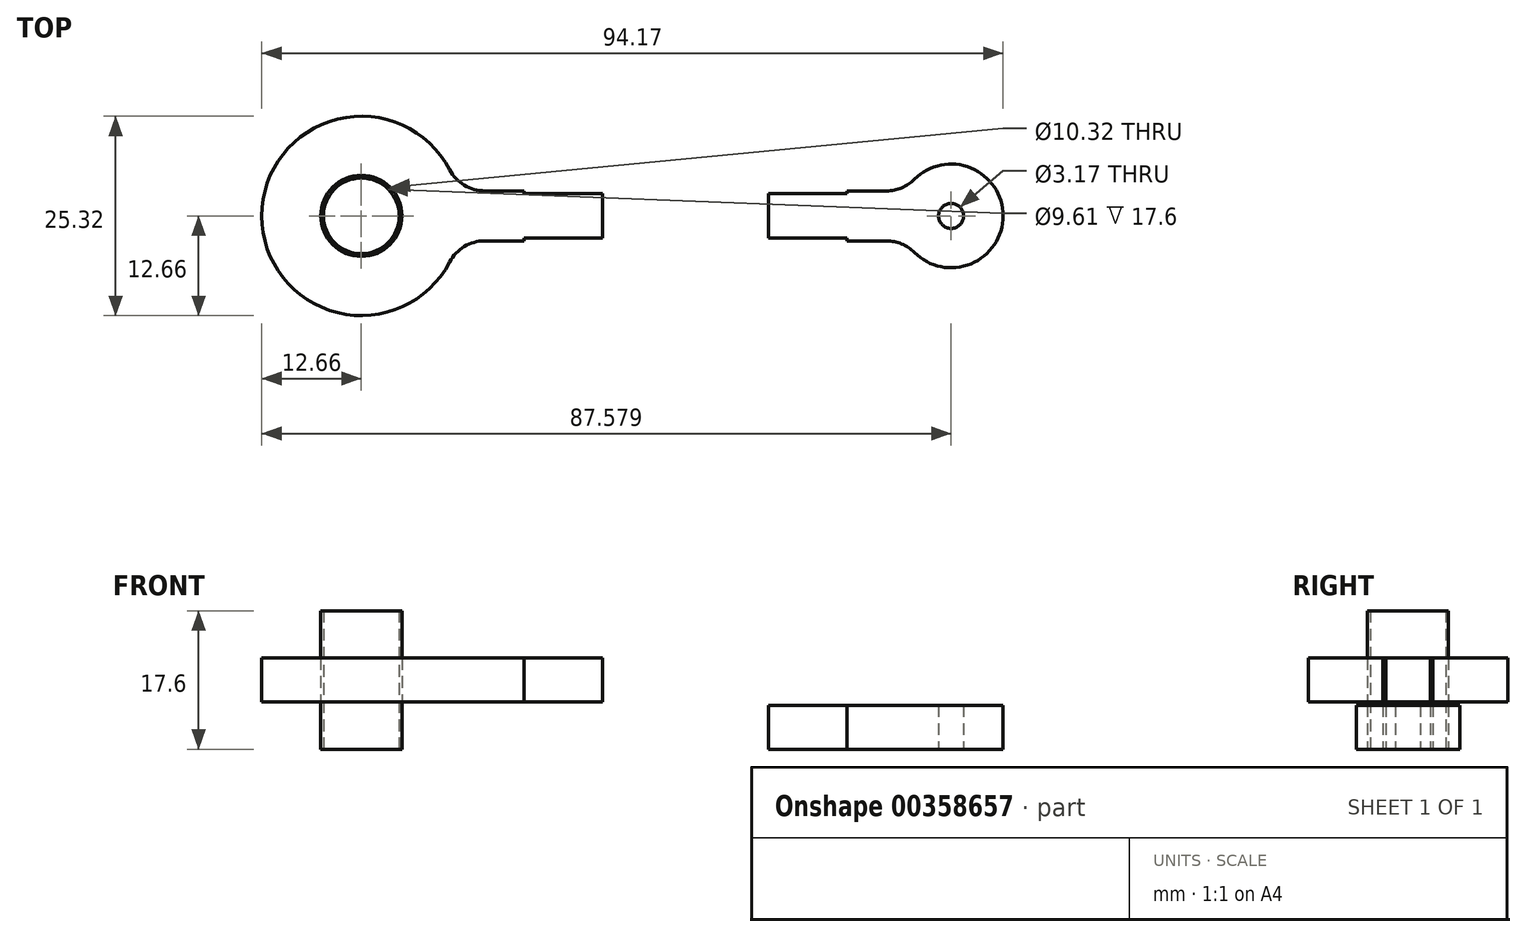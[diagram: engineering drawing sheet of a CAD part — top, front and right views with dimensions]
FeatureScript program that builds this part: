
annotation { "Feature Type Name" : "Feature", "Feature Type Description" : "" }
export const myFeature = defineFeature(function(context is Context, id is Id, definition is map)
    precondition{}
    {
        {
            var Q0;
            Q0=qCreatedBy(makeId("Top.planeOp"),FACE);
            var sketch = newSketch(context, id + "F0", { "sketchPlane" : qUnion([Q0])});
            skCircle(sketch, "E0", {"center": v(0, 0) * mm, "radius": 4.8 * mm});
            skCircle(sketch, "E1", {"center": v(0, 0) * mm, "radius": 5.16 * mm});
            skSolve(sketch);
        }
        {
            var Q0;
            Q0 = qSketchRegion(id + "F0", true);
            extrude(context, id + "F1", {"entities" : qUnion([Q0]), "depth" : (5.6 + 3 * 2 + 3 * 2) * mm, "offsetDistance" : 25 * mm});
        }
        {
            var Q0;
            Q0=qCreatedBy(makeId("Top.planeOp"),FACE);
            var sketch = newSketch(context, id + "F2", { "sketchPlane" : qUnion([Q0])});
            skCircle(sketch, "E2", {"center": v(0, 0) * mm, "radius": 5.16 * mm});
            skArc(sketch, "E3", {"start": v(11.22, 5.86) * mm, "mid": v(-12.66, 0) * mm, "end": v(11.22, -5.86) * mm});
            skLineSegment(sketch, "E4", {"start": v(0, 0) * mm, "end": v(90.69, 0) * mm, "construction": true});
            skLineSegment(sketch, "E5", {"start": v(15.65, 3.17) * mm, "end": v(20.65, 3.17) * mm});
            skLineSegment(sketch, "E6", {"start": v(20.65, 3.18) * mm, "end": v(20.65, 2.82) * mm});
            skLineSegment(sketch, "E7", {"start": v(20.65, 2.82) * mm, "end": v(30.65, 2.82) * mm});
            skLineSegment(sketch, "E8", {"start": v(30.65, 2.82) * mm, "end": v(30.65, -2.82) * mm});
            skLineSegment(sketch, "E9", {"start": v(30.65, -2.82) * mm, "end": v(20.65, -2.82) * mm});
            skLineSegment(sketch, "E10", {"start": v(20.65, -2.82) * mm, "end": v(20.65, -3.17) * mm});
            skLineSegment(sketch, "E11", {"start": v(20.65, -3.17) * mm, "end": v(15.65, -3.17) * mm});
            skArc(sketch, "E12", {"start": v(11.22, 5.86) * mm, "mid": v(13.06, 3.9) * mm, "end": v(15.65, 3.18) * mm});
            skArc(sketch, "E13", {"start": v(15.65, -3.17) * mm, "mid": v(13.06, -3.9) * mm, "end": v(11.22, -5.86) * mm});
            skLineSegment(sketch, "E14", {"start": v(51.7, 2.82) * mm, "end": v(61.7, 2.82) * mm});
            skLineSegment(sketch, "E15", {"start": v(51.7, -2.82) * mm, "end": v(61.7, -2.82) * mm});
            skLineSegment(sketch, "E16", {"start": v(61.7, -3.17) * mm, "end": v(66.7, -3.17) * mm});
            skLineSegment(sketch, "E17", {"start": v(51.7, 2.82) * mm, "end": v(51.7, -2.82) * mm});
            skLineSegment(sketch, "E18.trimOffspring", {"start": v(61.7, -2.82) * mm, "end": v(61.7, -3.17) * mm});
            skLineSegment(sketch, "E19", {"start": v(61.7, 3.17) * mm, "end": v(66.7, 3.17) * mm});
            skLineSegment(sketch, "E20", {"start": v(61.7, 2.82) * mm, "end": v(61.7, 3.18) * mm});
            skCircle(sketch, "E21", {"center": v(74.92, 0) * mm, "radius": 1.59 * mm});
            skArc(sketch, "E22", {"start": v(70.25, -4.65) * mm, "mid": v(81.5, 0) * mm, "end": v(70.25, 4.65) * mm});
            skArc(sketch, "E23", {"start": v(66.7, 3.18) * mm, "mid": v(68.63, 3.56) * mm, "end": v(70.25, 4.65) * mm});
            skArc(sketch, "E24", {"start": v(70.25, -4.65) * mm, "mid": v(68.63, -3.56) * mm, "end": v(66.7, -3.17) * mm});
            skSolve(sketch);
        }
        {
            var Q0;
            Q0 = qSketchRegion(id + "F2", true);
            extrude(context, id + "F3", {"entities" : qUnion([Q0]), "depth" : 5.6 * mm, "offsetDistance" : 25 * mm});
        }
        {
            var Q0;
            Q0=makeQuery(id+"F3.opExtrude","SWEPT_BODY",BODY,{"disambiguationData":[OSD([sQuery(id+"F2.wireOp",EDGE,"E2"),sQuery(id+"F2.wireOp",EDGE,"E3"),sQuery(id+"F2.wireOp",EDGE,"E5"),sQuery(id+"F2.wireOp",EDGE,"E6"),sQuery(id+"F2.wireOp",EDGE,"E7"),sQuery(id+"F2.wireOp",EDGE,"E8"),sQuery(id+"F2.wireOp",EDGE,"E9"),sQuery(id+"F2.wireOp",EDGE,"E10"),sQuery(id+"F2.wireOp",EDGE,"E11"),sQuery(id+"F2.wireOp",EDGE,"E12"),sQuery(id+"F2.wireOp",EDGE,"E13")])]});
            transform(context, id + "F4", {"entities" : qUnion([Q0]), "transformType" : TransformType.TRANSLATION_3D, "dx" : 0 * mm, "dy" : 0 * mm, "dz" : (17.6 / 2 - 5.6 / 2) * mm, "makeCopy" : false});
        }
    });
